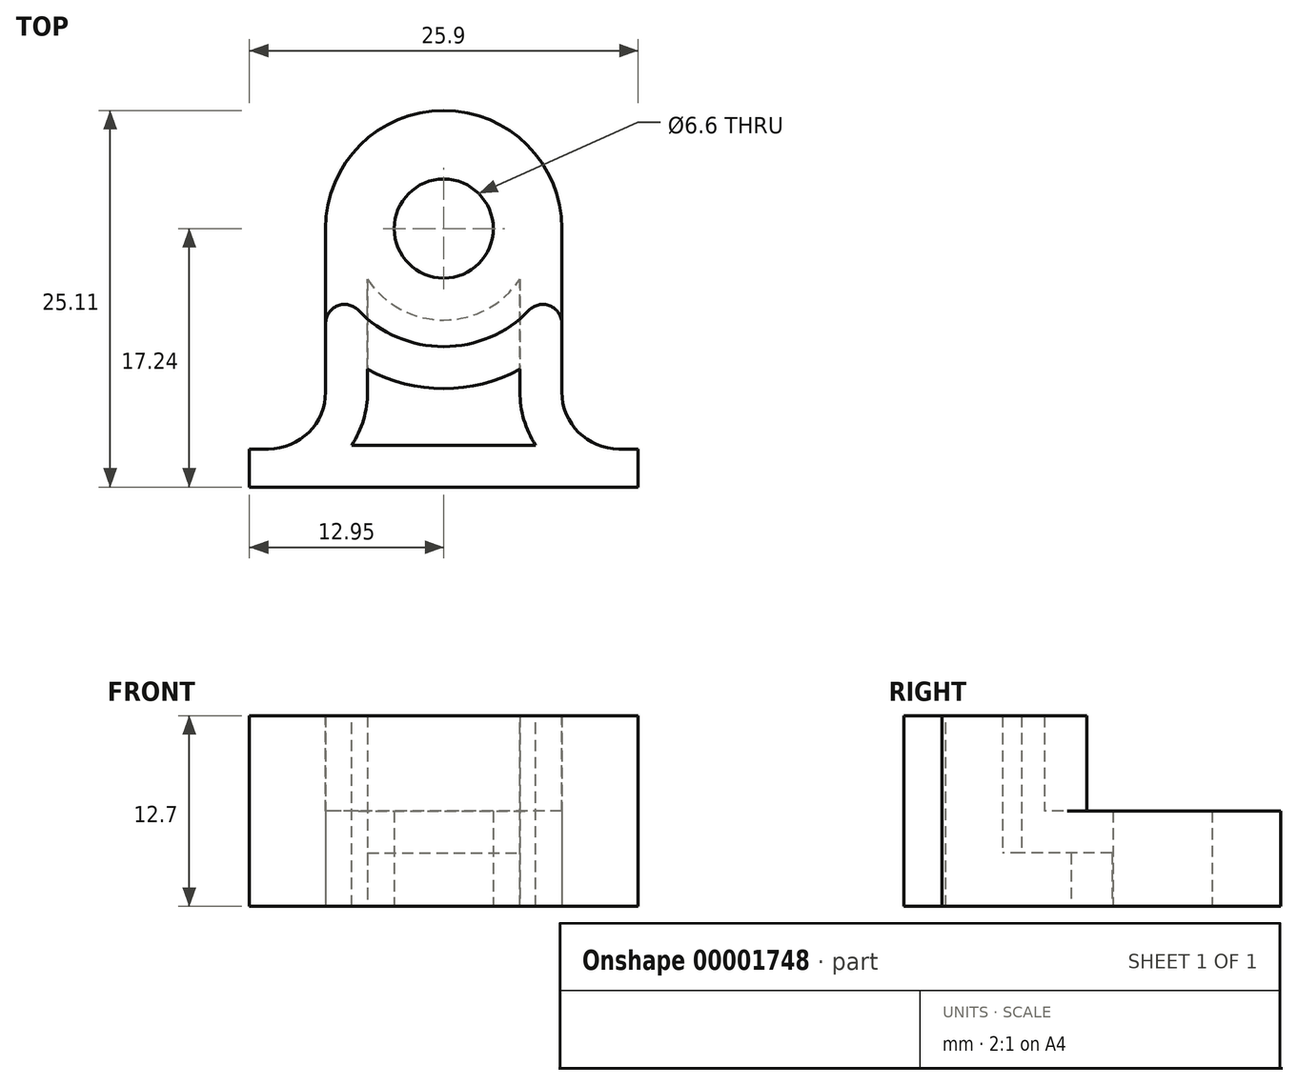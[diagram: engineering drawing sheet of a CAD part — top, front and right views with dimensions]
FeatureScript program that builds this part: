
annotation { "Feature Type Name" : "Feature", "Feature Type Description" : "" }
export const myFeature = defineFeature(function(context is Context, id is Id, definition is map)
    precondition{}
    {
        {
            var Q0;
            Q0=qCreatedBy(makeId("Top.planeOp"),FACE);
            var sketch = newSketch(context, id + "F0", { "sketchPlane" : qUnion([Q0])});
            skCircle(sketch, "E0", {"center": v(0, 0) * mm, "radius": 3.3 * mm});
            skSolve(sketch);
        }
        {
            var Q0;
            Q0=qCreatedBy(makeId("Top.planeOp"),FACE);
            var sketch = newSketch(context, id + "F1", { "sketchPlane" : qUnion([Q0])});
            skCircle(sketch, "E1", {"center": v(0, 0) * mm, "radius": 7.87 * mm});
            skSolve(sketch);
        }
        {
            var Q0;
            Q0=qCreatedBy(makeId("Top.planeOp"),FACE);
            var sketch = newSketch(context, id + "F2", { "sketchPlane" : qUnion([Q0])});
            skLineSegment(sketch, "E2", {"start": v(-7.87, 0) * mm, "end": v(-7.87, -14.7) * mm});
            skLineSegment(sketch, "E3", {"start": v(-7.87, -14.7) * mm, "end": v(7.87, -14.7) * mm});
            skLineSegment(sketch, "E4", {"start": v(7.87, -14.7) * mm, "end": v(7.87, 0) * mm});
            skArc(sketch, "E5", {"start": v(-7.87, 0) * mm, "mid": v(0, -7.87) * mm, "end": v(7.87, 0) * mm});
            skLineSegment(sketch, "E6", {"start": v(-7.87, -14.7) * mm, "end": v(-12.95, -14.7) * mm});
            skLineSegment(sketch, "E7", {"start": v(-12.95, -14.7) * mm, "end": v(-12.95, -17.24) * mm});
            skLineSegment(sketch, "E8", {"start": v(-12.95, -17.24) * mm, "end": v(12.95, -17.24) * mm});
            skLineSegment(sketch, "E9", {"start": v(12.95, -17.24) * mm, "end": v(12.95, -14.7) * mm});
            skLineSegment(sketch, "E10", {"start": v(12.95, -14.7) * mm, "end": v(7.87, -14.7) * mm});
            skSolve(sketch);
        }
        {
            var Q0;
            Q0=makeQuery(id+"F2.imprint","IMPRINT",FACE,{"disambiguationData":[TD([[makeQuery(id+"F2.imprint","IMPRINT",EDGE,{"derivedFrom":sQuery(id+"F2.wireOp",EDGE,"E3")}),-1.0]])]});
            var Q1;
            Q1=makeQuery(id+"F2.imprint","IMPRINT",FACE,{"disambiguationData":[TD([[makeQuery(id+"F2.imprint","IMPRINT",EDGE,{"derivedFrom":sQuery(id+"F2.wireOp",EDGE,"E2")}),1.0]])]});
            extrude(context, id + "F3", {"entities" : qUnion([Q0, Q1]), "depth" : 12.7 * mm});
        }
        {
            var Q0;
            Q0 = qSketchRegion(id + "F1", true);
            extrude(context, id + "F4", {"entities" : qUnion([Q0]), "operationType" : NewBodyOperationType.ADD, "depth" : 6.35 * mm});
        }
        {
            var Q0;
            Q0 = qSketchRegion(id + "F0", true);
            extrude(context, id + "F5", {"entities" : qUnion([Q0]), "operationType" : NewBodyOperationType.REMOVE, "depth" : 6.35 * mm});
        }
        {
            var Q0;
            Q0=makeQuery(id+"F3.opExtrude","SWEPT_EDGE",EDGE,{"disambiguationData":[OSD([sQuery(id+"F2.wireOp",EDGE,"E2"),sQuery(id+"F2.wireOp",EDGE,"E3"),sQuery(id+"F2.wireOp",EDGE,"E6")])]});
            var Q1;
            Q1=makeQuery(id+"F3.opExtrude","SWEPT_EDGE",EDGE,{"disambiguationData":[OSD([sQuery(id+"F2.wireOp",EDGE,"E3"),sQuery(id+"F2.wireOp",EDGE,"E4"),sQuery(id+"F2.wireOp",EDGE,"E10")])]});
            fillet(context, id + "F6", {"entities" : qUnion([Q0, Q1]), "radius" : 3.8 * mm, "tangentPropagation" : true, "allowEdgeOverflow" : false});
        }
        {
            var Q0;
            {var subQ0=sQuery(id+"F2.wireOp",EDGE,"E2");var subQ1=sQuery(id+"F2.wireOp",EDGE,"E5");Q0=makeQuery(id+"F4.boolean.opBoolean","SPLIT",EDGE,{"disambiguationData":[TD([makeQuery(id+"F3.opExtrude","CAP_FACE",FACE,{"disambiguationData":[OSD([subQ0,sQuery(id+"F2.wireOp",EDGE,"E4"),subQ1,sQuery(id+"F2.wireOp",EDGE,"E6"),sQuery(id+"F2.wireOp",EDGE,"E7"),sQuery(id+"F2.wireOp",EDGE,"E8"),sQuery(id+"F2.wireOp",EDGE,"E9"),sQuery(id+"F2.wireOp",EDGE,"E10")])],"isStart":false})])],"derivedFrom":makeQuery(id+"F3.opExtrude","SWEPT_EDGE",EDGE,{"disambiguationData":[OSD([subQ0,subQ1])]})});}
            var Q1;
            {var subQ0=sQuery(id+"F2.wireOp",EDGE,"E4");var subQ1=sQuery(id+"F2.wireOp",EDGE,"E5");Q1=makeQuery(id+"F4.boolean.opBoolean","SPLIT",EDGE,{"disambiguationData":[TD([makeQuery(id+"F3.opExtrude","CAP_FACE",FACE,{"disambiguationData":[OSD([sQuery(id+"F2.wireOp",EDGE,"E2"),subQ0,subQ1,sQuery(id+"F2.wireOp",EDGE,"E6"),sQuery(id+"F2.wireOp",EDGE,"E7"),sQuery(id+"F2.wireOp",EDGE,"E8"),sQuery(id+"F2.wireOp",EDGE,"E9"),sQuery(id+"F2.wireOp",EDGE,"E10")])],"isStart":false})])],"derivedFrom":makeQuery(id+"F3.opExtrude","SWEPT_EDGE",EDGE,{"disambiguationData":[OSD([subQ0,subQ1])]})});}
            fillet(context, id + "F7", {"entities" : qUnion([Q0, Q1]), "radius" : 1.27 * mm, "tangentPropagation" : true, "allowEdgeOverflow" : false});
        }
        {
            var Q0;
            Q0=makeQuery(id+"F3.opExtrude","CAP_FACE",FACE,{"disambiguationData":[OSD([sQuery(id+"F2.wireOp",EDGE,"E2"),sQuery(id+"F2.wireOp",EDGE,"E4"),sQuery(id+"F2.wireOp",EDGE,"E5"),sQuery(id+"F2.wireOp",EDGE,"E6"),sQuery(id+"F2.wireOp",EDGE,"E7"),sQuery(id+"F2.wireOp",EDGE,"E8"),sQuery(id+"F2.wireOp",EDGE,"E9"),sQuery(id+"F2.wireOp",EDGE,"E10")])],"isStart":false});
            shell(context, id + "F8", {"entities" : qUnion([Q0]), "thickness" : 2.8 * mm});
        }
        {
            var Q0;
            Q0=makeQuery(id+"F8.opShell","OFFSET_FACE",FACE,{"disambiguationData":[OSD([sQuery(id+"F1.wireOp",EDGE,"E1"),sQuery(id+"F2.wireOp",EDGE,"E2"),sQuery(id+"F2.wireOp",EDGE,"E4"),sQuery(id+"F2.wireOp",EDGE,"E5"),sQuery(id+"F2.wireOp",EDGE,"E6"),sQuery(id+"F2.wireOp",EDGE,"E7"),sQuery(id+"F2.wireOp",EDGE,"E8"),sQuery(id+"F2.wireOp",EDGE,"E9"),sQuery(id+"F2.wireOp",EDGE,"E10")])]});
            extrude(context, id + "F9", {"entities" : qUnion([Q0]), "operationType" : NewBodyOperationType.REMOVE, "oppositeDirection" : true, "depth" : 25.4 * mm});
        }
    });
